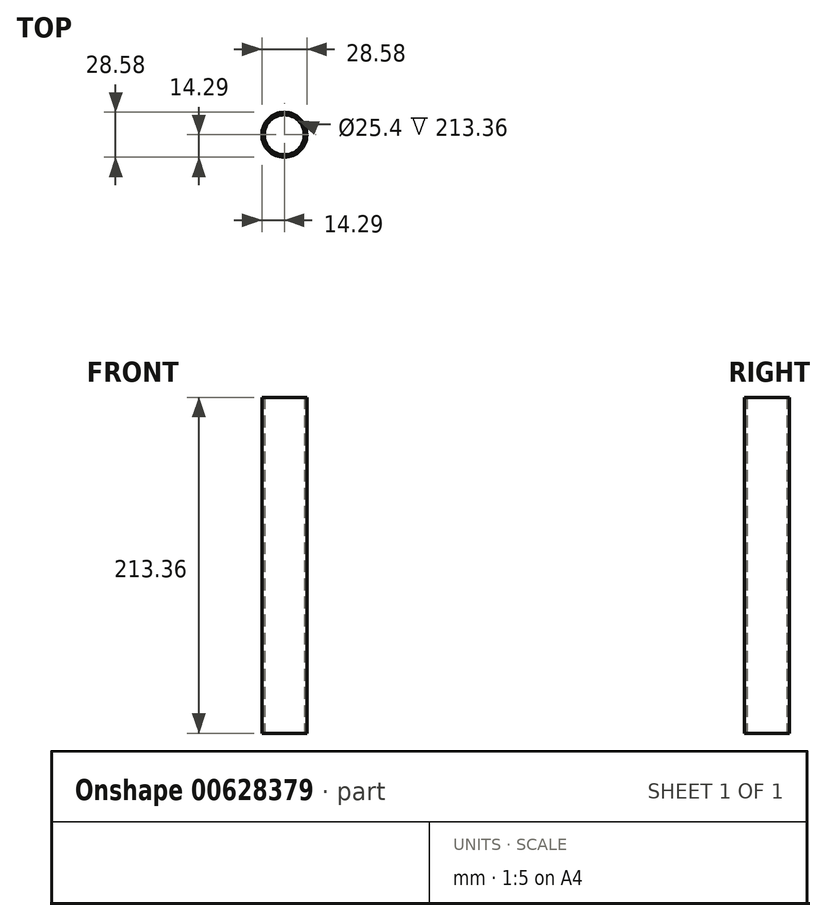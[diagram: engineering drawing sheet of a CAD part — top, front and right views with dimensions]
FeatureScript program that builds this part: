
annotation { "Feature Type Name" : "Feature", "Feature Type Description" : "" }
export const myFeature = defineFeature(function(context is Context, id is Id, definition is map)
    precondition{}
    {
        {
            var Q0;
            Q0=qCreatedBy(makeId("Top.planeOp"),FACE);
            var sketch = newSketch(context, id + "F0", { "sketchPlane" : qUnion([Q0])});
            skLineSegment(sketch, "E0", {"start": v(0, 0) * mm, "end": v(12.7, 0) * mm});
            skCircle(sketch, "E1", {"center": v(0, 0) * mm, "radius": 12.7 * mm});
            skCircle(sketch, "E2.0", {"center": v(0, 0) * mm, "radius": 14.29 * mm});
            skSolve(sketch);
        }
        {
            var Q0;
            Q0=qCreatedBy(makeId("Top.planeOp"),FACE);
            var sketch = newSketch(context, id + "F1", { "sketchPlane" : qUnion([Q0])});
            skSolve(sketch);
        }
        {
            var Q0;
            Q0=qSketchRegion(id+"F1",true);
            var Q1;
            Q1=makeQuery(id+"F0.imprint","IMPRINT",FACE,{"disambiguationData":[TD([[makeQuery(id+"F0.imprint","IMPRINT",EDGE,{"derivedFrom":sQuery(id+"F0.wireOp",EDGE,"E1")}),-1.0]])]});
            extrude(context, id + "F2", {"entities" : qUnion([Q0, Q1]), "depth" : 213.36 * mm, "offsetDistance" : 25.4 * mm});
        }
    });
